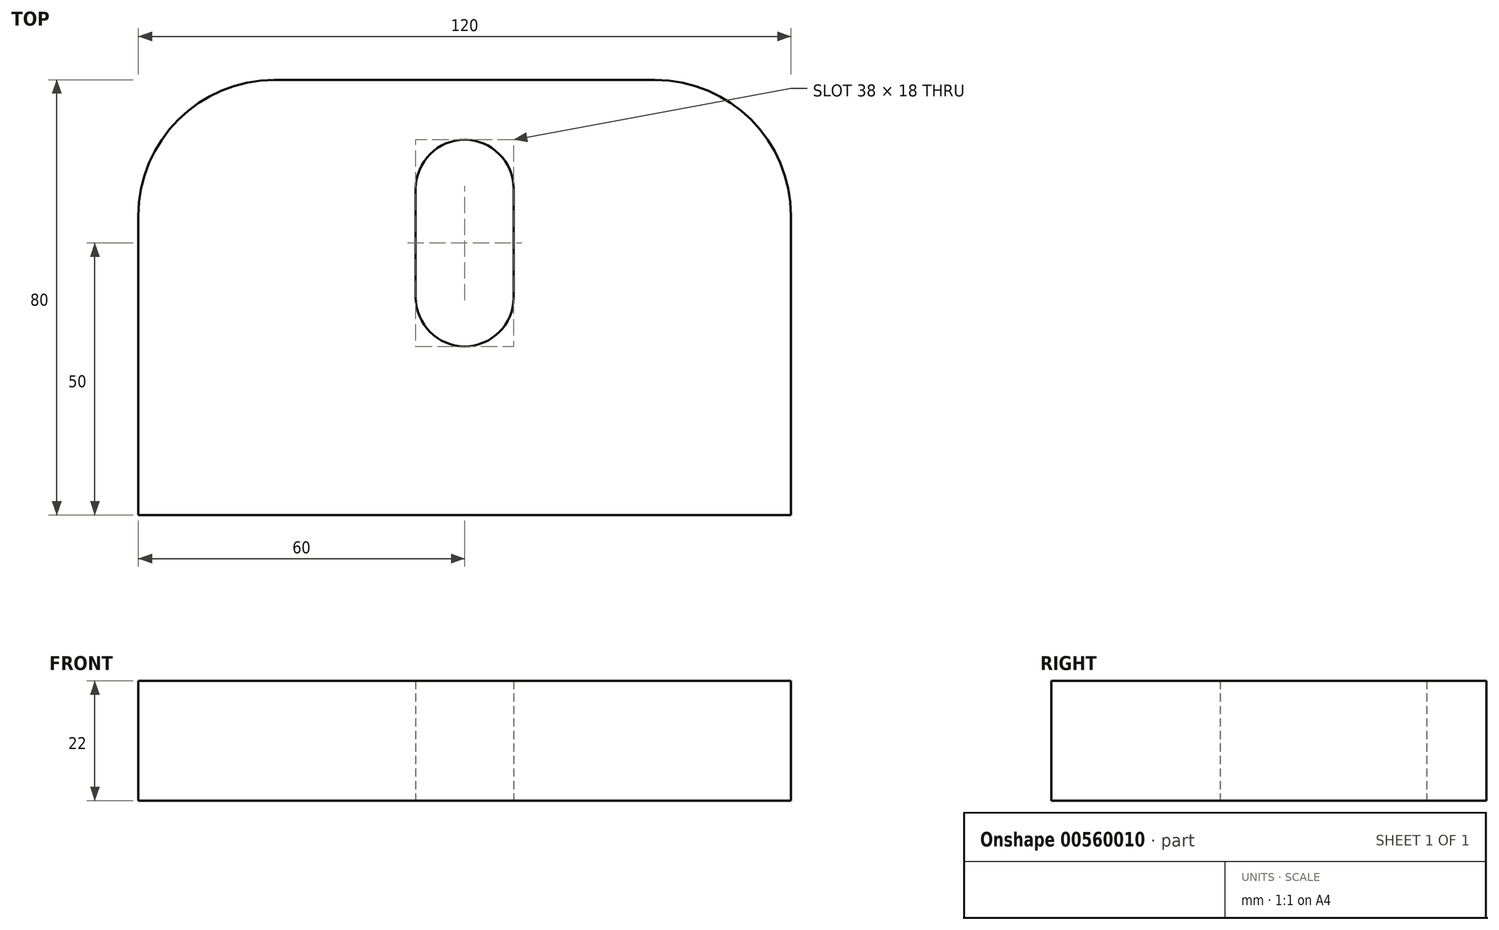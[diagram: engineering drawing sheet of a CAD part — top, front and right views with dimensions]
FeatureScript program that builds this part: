
annotation { "Feature Type Name" : "Feature", "Feature Type Description" : "" }
export const myFeature = defineFeature(function(context is Context, id is Id, definition is map)
    precondition{}
    {
        {
            var Q0;
            Q0=qCreatedBy(makeId("Top.planeOp"),FACE);
            var sketch = newSketch(context, id + "F0", { "sketchPlane" : qUnion([Q0])});
            skLineSegment(sketch, "E0.bottom", {"start": v(35, 40) * mm, "end": v(-35, 40) * mm});
            skLineSegment(sketch, "E0.top", {"start": v(60, -40) * mm, "end": v(-60, -40) * mm});
            skLineSegment(sketch, "E0.left", {"start": v(60, 15) * mm, "end": v(60, -40) * mm});
            skLineSegment(sketch, "E0.right", {"start": v(-60, 15) * mm, "end": v(-60, -40) * mm});
            skPoint(sketch, "E0.middle", {"position": v(0, 0) * mm});
            skPoint(sketch, "E1.visualSharp", {"position": v(-60, 40) * mm});
            skArc(sketch, "E1.filletArc", {"start": v(-35, 40) * mm, "mid": v(-52.68, 32.68) * mm, "end": v(-60, 15) * mm});
            skPoint(sketch, "E2.visualSharp", {"position": v(60, 40) * mm});
            skArc(sketch, "E2.filletArc", {"start": v(60, 15) * mm, "mid": v(52.68, 32.68) * mm, "end": v(35, 40) * mm});
            skPoint(sketch, "E3.endSnap0", {"position": v(0, 40) * mm});
            skArc(sketch, "E4", {"start": v(9, 20) * mm, "mid": v(0, 29) * mm, "end": v(-9, 20) * mm});
            skArc(sketch, "E5", {"start": v(-9, 0) * mm, "mid": v(0, -9) * mm, "end": v(9, 0) * mm});
            skLineSegment(sketch, "E6.left", {"start": v(-9, 0) * mm, "end": v(-9, 20) * mm});
            skLineSegment(sketch, "E6.right", {"start": v(9, 0) * mm, "end": v(9, 20) * mm});
            skSolve(sketch);
        }
        {
            var Q0;
            Q0=makeQuery(id+"F0.imprint","IMPRINT",FACE,{"disambiguationData":[TD([[makeQuery(id+"F0.imprint","IMPRINT",EDGE,{"derivedFrom":sQuery(id+"F0.wireOp",EDGE,"E0.bottom")}),1.0]])]});
            extrude(context, id + "F1", {"entities" : qUnion([Q0]), "depth" : 22 * mm, "offsetDistance" : 25 * mm});
        }
    });
